# Revit family: Gira_202800
name_source: partatom
category: Allgemeines Modell
revit_build: Autodesk Revit 2017 (Build: 20160225_1515(x64)
units: mm (PartAtom-declared; Revit-internal decimal feet)

## family parameters
Basisbauteil = Fläche
Beim Laden mit Abzugskörper schneiden = Nein
Bemaßung runder Anschluss = Durchmesser verwenden
Gemeinsam genutzt = Nein
Kann Basisbauteil für Bewehrung sein = Nein
Raumberechnungspunkt = Nein
Teiletyp = Normal

## types (1)
- Gira_202800
    Andere Bussysteme = ohne
    Anschlussart = Schraubklemme
    App-Steuerung über Bluetooth = Nein
    BIM = https://media.stage.bim.site
    Bedienungsart = Dreh-/Druckknopf
    Befestigungsart = Befestigung mit Schraube
    Beschreibung = DALI-Potentiometer mit integriertem Netzteil   Merkmale: - Schalten und Helligkeitseinstellung für Leuchten mit DALI-Schnittstelle. - Integrierte Spannungsversorgung nach DALI-Spezifikation (DIN IEC 60926) für 26 DALI-Teilnehmer. - Parallelschalten von bis zu 4 DALI-Potentiometern mit integriertem Netzteil um bis zu 104 DALI-Teilnehmer zu versorgen. - Bedienung kann von mehreren Bedienstellen aus parallel erfolgen. Kommunikation erfolgt über Broadcast. - Speichern einer Grund- bzw. Einschalthelligkeit.  Hinweise : - Bei der Auswahl der DALI-Spannungsversorgung ist stets die Anzahl der DALI-Teilnehmer und des DALI-Potentiometers (gilt immer als 1 Teilnehmer) zu berücksichtigen.
    Bussystem Funkbus = Nein
    Bussystem KNX = Ja
    Bussystem KNX-Funk = Nein
    Bussystem LON = Nein
    Bussystem Powernet = Nein
    Datenblatt = https://katalog.gira.de
    Dimmung Phasenabschnitt = Nein
    Dimmung Phasenanschnitt = Nein
    Farbe = sonstige
    Frequenz [Hz] = [50:60]
    Funk bidirektional = Nein
    GTIN = 4010337023456
    Geeignet für Schutzart (IP) = IP20
    HAN = 202800
    Halogenfrei = Nein
    Hersteller = Gira
    Lastart = sonstige
    Lichtwertspeicher = Nein
    Montageart = Unterputz
    Nebenstelleneingang = Nein
    Nennspannung [Volt] = [230:230]
    Oberfläche = sonstige
    Produktseite = http://katalog.gira.de
    Seriendimmer = Nein
    Transparent = Nein
    Typname = DALI-Potentiometer Netzteil Einsatz
    URL = https://www.gira.de
    Verwendbar mit Bewegungsmelder = Nein
    Verwendbar mit Funktaste = Nein
    Verwendbar mit IR-Taste = Nein
    Verwendbar mit Präsenzmelder = Nein
    Verwendbar mit Taste = Ja
    Verwendbar mit Zeitschalter/Timer = Nein
    Vorgabe-Ansicht = 1219 mm
    Werkstoff = sonstige
    Werkstoffgüte = sonstige
    Zusammenstellung = Basiselement

## geometry (parser evidence)
native form markers: Sweep x2
no freeform markers — native parametric forms only
